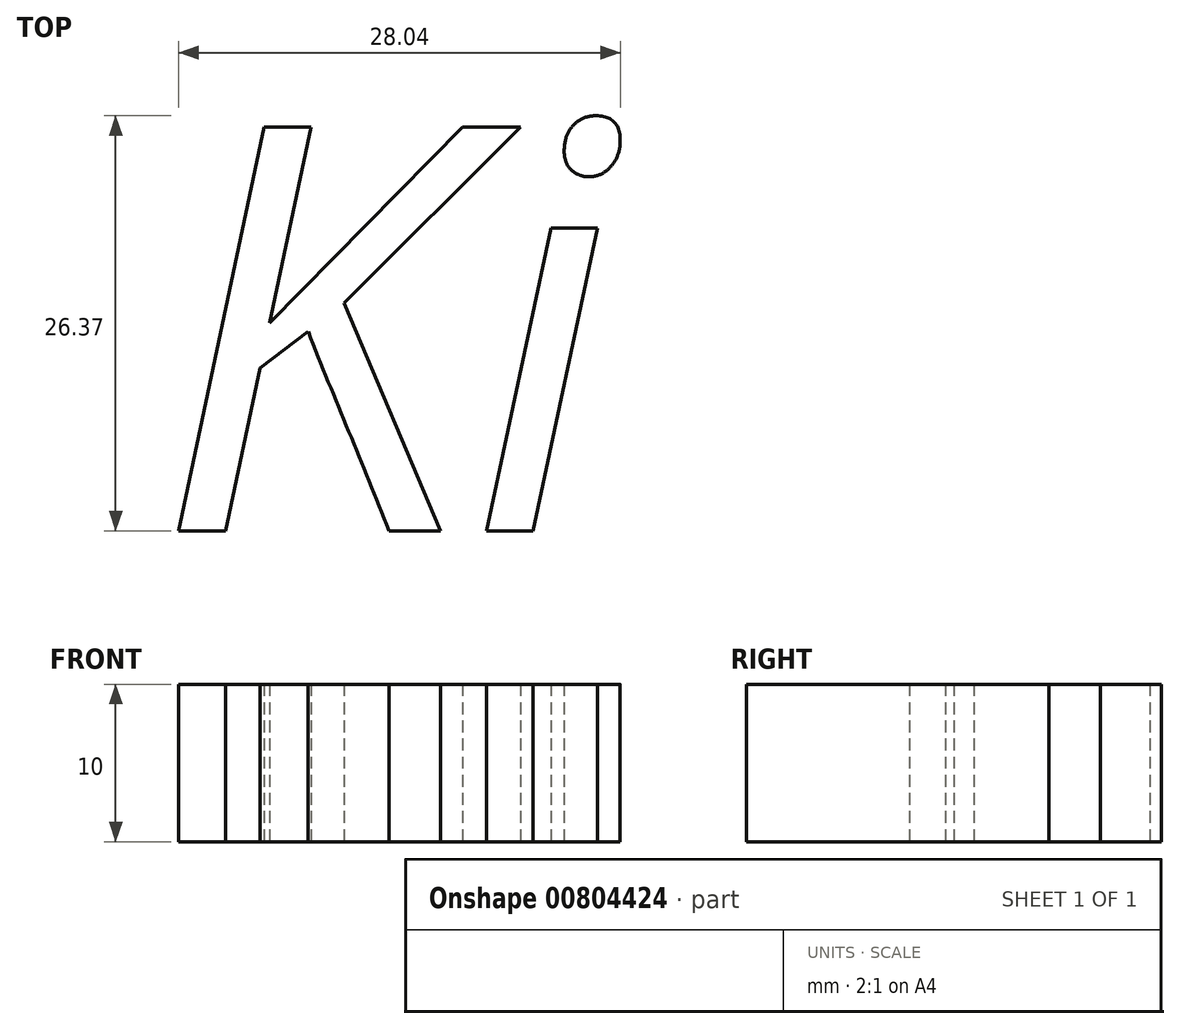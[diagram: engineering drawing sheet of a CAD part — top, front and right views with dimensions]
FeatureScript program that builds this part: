
annotation { "Feature Type Name" : "Feature", "Feature Type Description" : "" }
export const myFeature = defineFeature(function(context is Context, id is Id, definition is map)
    precondition{}
    {
        {
            var Q0;
            Q0=qCreatedBy(makeId("Top.planeOp"),FACE);
            var sketch = newSketch(context, id + "F0", { "sketchPlane" : qUnion([Q0])});
            skText(sketch, "E0", { "text": "Ki", "fontName": "OpenSans-Italic.ttf"});
            const initialGuessF0  = {"E0": [-0.0493, 0.01107, 1, 0, 0.02587]};
            skSetInitialGuess(sketch, initialGuessF0);
            skSolve(sketch);
        }
        {
            var Q0;
            Q0 = qSketchRegion(id + "F0", true);
            extrude(context, id + "F1", {"entities" : qUnion([Q0]), "depth" : 10 * mm, "offsetDistance" : 25 * mm});
        }
    });
